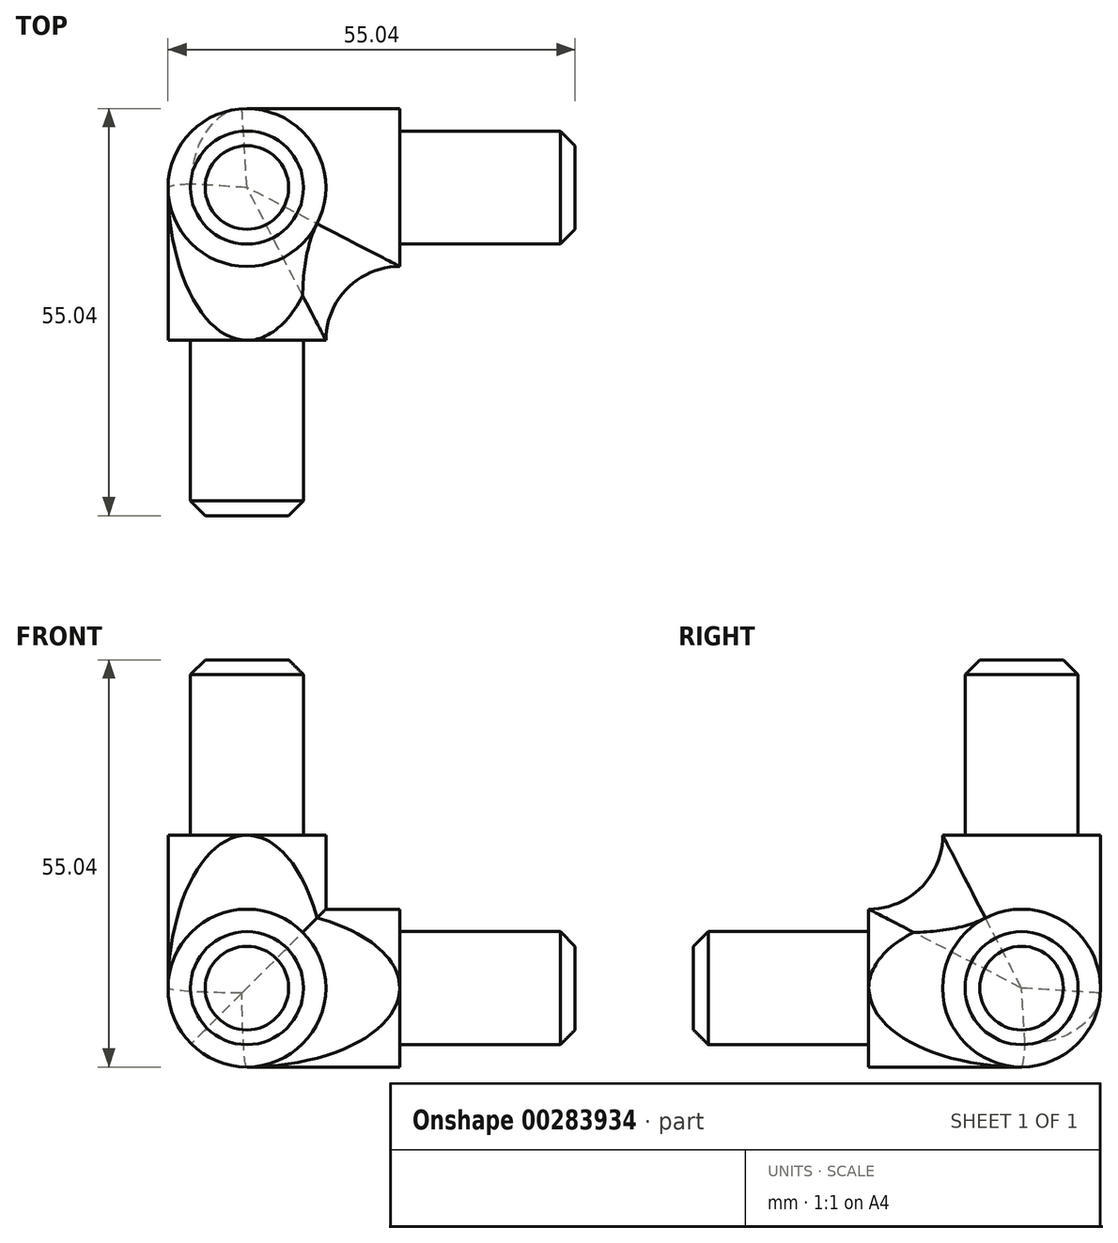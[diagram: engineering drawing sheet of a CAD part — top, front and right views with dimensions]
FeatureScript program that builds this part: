
annotation { "Feature Type Name" : "Feature", "Feature Type Description" : "" }
export const myFeature = defineFeature(function(context is Context, id is Id, definition is map)
    precondition{}
    {
        {
            var Q0;
            Q0=qCreatedBy(makeId("Front.planeOp"),FACE);
            var sketch = newSketch(context, id + "F0", { "sketchPlane" : qUnion([Q0])});
            skCircle(sketch, "E0", {"center": v(0, 0) * mm, "radius": 10.67 * mm});
            skSolve(sketch);
        }
        {
            var Q0;
            Q0 = qSketchRegion(id + "F0", true);
            extrude(context, id + "F1", {"entities" : qUnion([Q0]), "depth" : 21.34 * mm / 2 + 10 * mm});
        }
        {
            var Q0;
            Q0=qCreatedBy(makeId("Top.planeOp"),FACE);
            var sketch = newSketch(context, id + "F2", { "sketchPlane" : qUnion([Q0])});
            skCircle(sketch, "E1", {"center": v(0, 0) * mm, "radius": 10.67 * mm});
            skSolve(sketch);
        }
        {
            var Q0;
            Q0 = qSketchRegion(id + "F2", true);
            extrude(context, id + "F3", {"entities" : qUnion([Q0]), "operationType" : NewBodyOperationType.ADD, "depth" : 21.34 * mm / 2 + 10 * mm});
        }
        {
            var Q0;
            Q0=qCreatedBy(makeId("Right.planeOp"),FACE);
            var sketch = newSketch(context, id + "F4", { "sketchPlane" : qUnion([Q0])});
            skCircle(sketch, "E2", {"center": v(0, 0) * mm, "radius": 10.67 * mm});
            skSolve(sketch);
        }
        {
            var Q0;
            Q0 = qSketchRegion(id + "F4", true);
            extrude(context, id + "F5", {"entities" : qUnion([Q0]), "operationType" : NewBodyOperationType.ADD, "depth" : 21.34 * mm / 2 + 10 * mm});
        }
        {
            var Q0;
            Q0=makeQuery(id+"F1.opExtrude","CAP_FACE",FACE,{"disambiguationData":[OSD([sQuery(id+"F0.wireOp",EDGE,"E0")])],"isStart":true});
            var Q1;
            Q1=makeQuery(id+"F3.opExtrude","SWEPT_FACE",FACE,{"disambiguationData":[OSD([sQuery(id+"F2.wireOp",EDGE,"E1")])]});
            extrude(context, id + "F6", {"entities" : qUnion([Q0]), "operationType" : NewBodyOperationType.ADD, "endBound" : BoundingType.UP_TO_SURFACE, "endBoundEntityFace" : qUnion([Q1]), "depth" : 25 * mm});
        }
        {
            var Q0;
            Q0=makeQuery(id+"F6.opExtrude","SWEPT_FACE",FACE,{"disambiguationData":[OSD([sQuery(id+"F0.wireOp",EDGE,"E0"),sQuery(id+"F4.wireOp",EDGE,"E2")])]});
            extrude(context, id + "F7", {"entities" : qUnion([Q0]), "operationType" : NewBodyOperationType.REMOVE, "endBound" : BoundingType.THROUGH_ALL, "oppositeDirection" : true, "depth" : 25 * mm});
        }
        {
            var Q0;
            Q0=makeQuery(id+"F5.opExtrude","CAP_FACE",FACE,{"disambiguationData":[OSD([sQuery(id+"F4.wireOp",EDGE,"E2")])],"isStart":false});
            var sketch = newSketch(context, id + "F8", { "sketchPlane" : qUnion([Q0])});
            skCircle(sketch, "E3", {"center": v(0, 0) * mm, "radius": 7.65 * mm});
            skSolve(sketch);
        }
        {
            var Q0;
            Q0 = qSketchRegion(id + "F8", true);
            extrude(context, id + "F9", {"entities" : qUnion([Q0]), "operationType" : NewBodyOperationType.ADD, "depth" : 1.5 * 15.8 * mm});
        }
        {
            var Q0;
            Q0=makeQuery(id+"F1.opExtrude","CAP_FACE",FACE,{"disambiguationData":[OSD([sQuery(id+"F0.wireOp",EDGE,"E0")])],"isStart":false});
            var sketch = newSketch(context, id + "F10", { "sketchPlane" : qUnion([Q0])});
            skCircle(sketch, "E4", {"center": v(0, 0) * mm, "radius": 7.65 * mm});
            skSolve(sketch);
        }
        {
            var Q0;
            Q0 = qSketchRegion(id + "F10", true);
            extrude(context, id + "F11", {"entities" : qUnion([Q0]), "operationType" : NewBodyOperationType.ADD, "depth" : 1.5 * 15.8 * mm});
        }
        {
            var Q0;
            Q0=makeQuery(id+"F3.opExtrude","CAP_FACE",FACE,{"disambiguationData":[OSD([sQuery(id+"F2.wireOp",EDGE,"E1")])],"isStart":false});
            var sketch = newSketch(context, id + "F12", { "sketchPlane" : qUnion([Q0])});
            skCircle(sketch, "E5", {"center": v(0, 0) * mm, "radius": 7.65 * mm});
            skSolve(sketch);
        }
        {
            var Q0;
            Q0 = qSketchRegion(id + "F12", true);
            extrude(context, id + "F13", {"entities" : qUnion([Q0]), "operationType" : NewBodyOperationType.ADD, "depth" : 1.5 * 15.8 * mm});
        }
        {
            var Q0;
            Q0=makeQuery(id+"F13.opExtrude","CAP_EDGE",EDGE,{"disambiguationData":[OSD([sQuery(id+"F12.wireOp",EDGE,"E5")])],"isStart":false});
            var Q1;
            Q1=makeQuery(id+"F9.opExtrude","CAP_EDGE",EDGE,{"disambiguationData":[OSD([sQuery(id+"F8.wireOp",EDGE,"E3")])],"isStart":false});
            var Q2;
            Q2=makeQuery(id+"F11.opExtrude","CAP_EDGE",EDGE,{"disambiguationData":[OSD([sQuery(id+"F10.wireOp",EDGE,"E4")])],"isStart":false});
            chamfer(context, id + "F14", {"entities" : qUnion([Q0, Q1, Q2]), "width" : 2 * mm, "tangentPropagation" : true});
        }
        {
            var Q0;
            {var subQ0=sQuery(id+"F0.wireOp",EDGE,"E0");Q0=makeQuery(id+"F7.boolean.opBoolean","INTERSECT",EDGE,{"derivedFrom":[makeQuery(id+"F6.boolean.opBoolean","MERGE",FACE,{"derivedFrom":[makeQuery(id+"F1.opExtrude","SWEPT_FACE",FACE,{"disambiguationData":[OSD([subQ0])]}),makeQuery(id+"F6.opExtrude","SWEPT_FACE",FACE,{"disambiguationData":[OSD([subQ0])]})]}),makeQuery(id+"F7.opExtrude","SWEPT_FACE",FACE,{"disambiguationData":[OSD([sQuery(id+"F4.wireOp",EDGE,"E2")])]})]});}
            fillet(context, id + "F15", {"entities" : qUnion([Q0]), "radius" : 10 * mm, "tangentPropagation" : true, "allowEdgeOverflow" : false});
        }
        {
            var Q0;
            {var subQ0=makeQuery(id+"F3.opExtrude","SWEPT_FACE",FACE,{"disambiguationData":[OSD([sQuery(id+"F2.wireOp",EDGE,"E1")])]});var subQ1=sQuery(id+"F0.wireOp",EDGE,"E0");Q0=makeQuery(id+"F6.boolean.opBoolean","MERGE",EDGE,{"derivedFrom":[makeQuery(id+"F3.boolean.opBoolean","INTERSECT",EDGE,{"derivedFrom":[makeQuery(id+"F1.opExtrude","SWEPT_FACE",FACE,{"disambiguationData":[OSD([subQ1])]}),subQ0]}),makeQuery(id+"F6.opExtrude","TWEAK_EDGE",EDGE,{"derivedFrom":[makeQuery(id+"F1.opExtrude","CAP_EDGE",EDGE,{"disambiguationData":[OSD([subQ1])],"isStart":true}),subQ0]})]});}
            fillet(context, id + "F16", {"entities" : qUnion([Q0]), "radius" : 10 * mm, "tangentPropagation" : true, "allowEdgeOverflow" : false});
        }
    });
